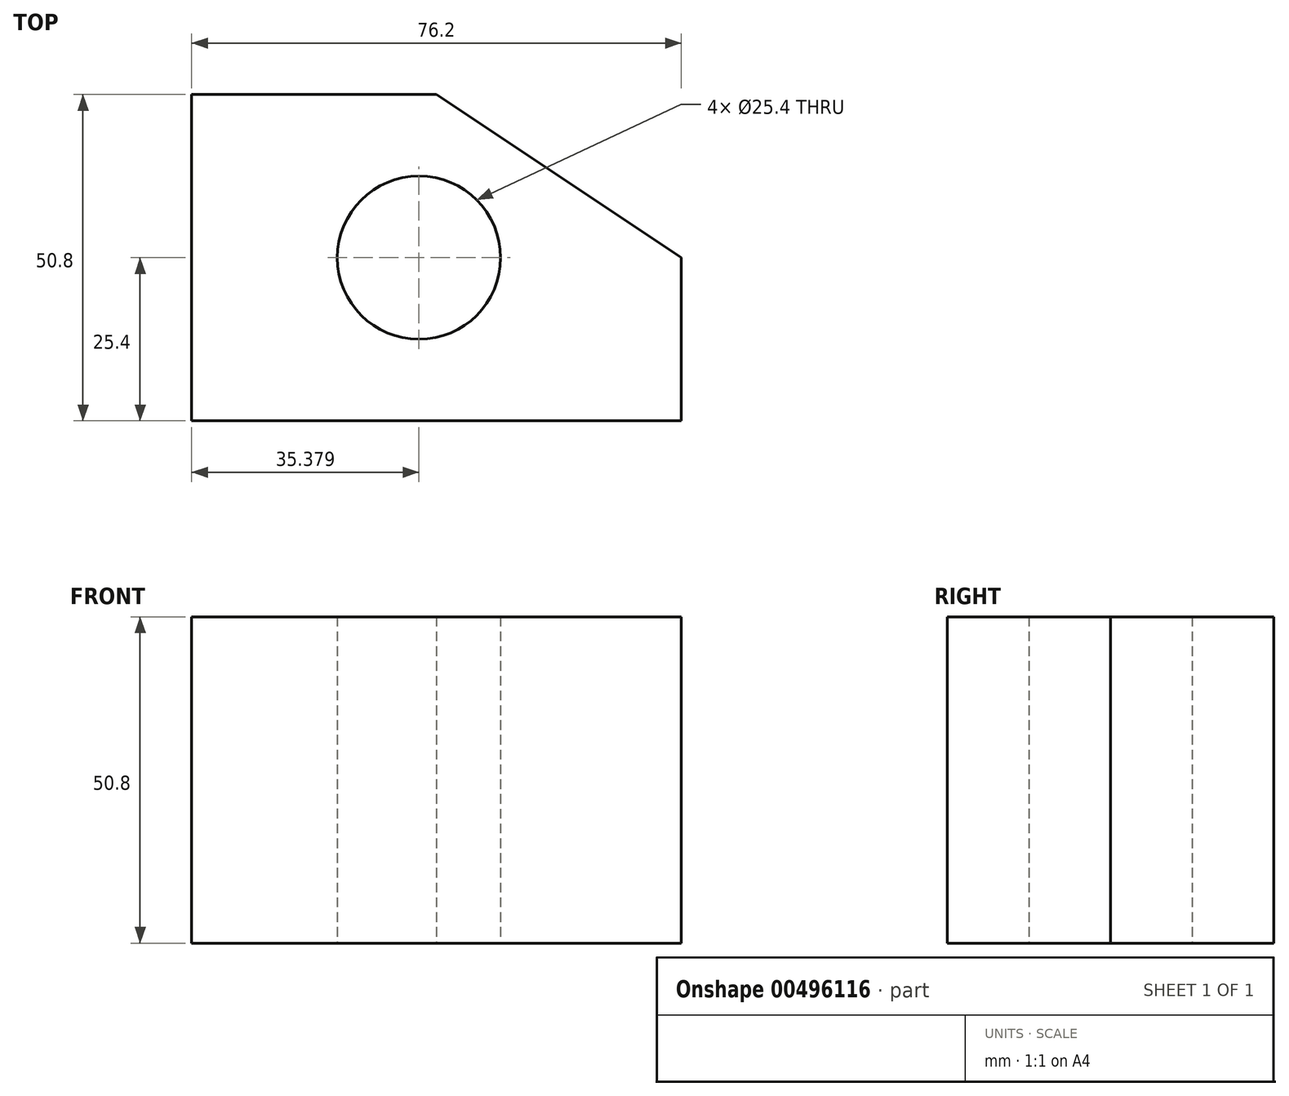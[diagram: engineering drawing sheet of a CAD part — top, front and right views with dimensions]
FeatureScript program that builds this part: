
annotation { "Feature Type Name" : "Feature", "Feature Type Description" : "" }
export const myFeature = defineFeature(function(context is Context, id is Id, definition is map)
    precondition{}
    {
        {
            var Q0;
            Q0=qCreatedBy(makeId("Top.planeOp"),FACE);
            var sketch = newSketch(context, id + "F0", { "sketchPlane" : qUnion([Q0])});
            skLineSegment(sketch, "E0", {"start": v(0, 0) * mm, "end": v(76.2, 0) * mm});
            skLineSegment(sketch, "E1", {"start": v(0, 0) * mm, "end": v(0, 50.8) * mm});
            skLineSegment(sketch, "E2", {"start": v(0, 50.8) * mm, "end": v(38.1, 50.8) * mm});
            skLineSegment(sketch, "E3", {"start": v(76.2, 0) * mm, "end": v(76.2, 25.4) * mm});
            skLineSegment(sketch, "E4", {"start": v(38.1, 50.8) * mm, "end": v(76.2, 25.4) * mm});
            skSolve(sketch);
        }
        {
            var Q0;
            Q0=qCreatedBy(makeId("Top.planeOp"),FACE);
            var sketch = newSketch(context, id + "F1", { "sketchPlane" : qUnion([Q0])});
            skCircle(sketch, "E5", {"center": v(35.38, 25.4) * mm, "radius": 12.7 * mm});
            skSolve(sketch);
        }
        {
            var Q0;
            Q0=makeQuery(id+"F0.imprint","IMPRINT",FACE,{"disambiguationData":[TD([[makeQuery(id+"F0.imprint","IMPRINT",EDGE,{"derivedFrom":sQuery(id+"F0.wireOp",EDGE,"E0")}),1.0]])]});
            extrude(context, id + "F2", {"entities" : qUnion([Q0]), "depth" : 50.8 * mm});
        }
        {
            var Q0;
            Q0=makeQuery(id+"F1.imprint","IMPRINT",FACE,{"disambiguationData":[TD([[makeQuery(id+"F1.imprint","IMPRINT",EDGE,{"derivedFrom":sQuery(id+"F1.wireOp",EDGE,"E5")}),1.0]])]});
            extrude(context, id + "F3", {"entities" : qUnion([Q0]), "operationType" : NewBodyOperationType.REMOVE, "depth" : 50.8 * mm});
        }
    });
